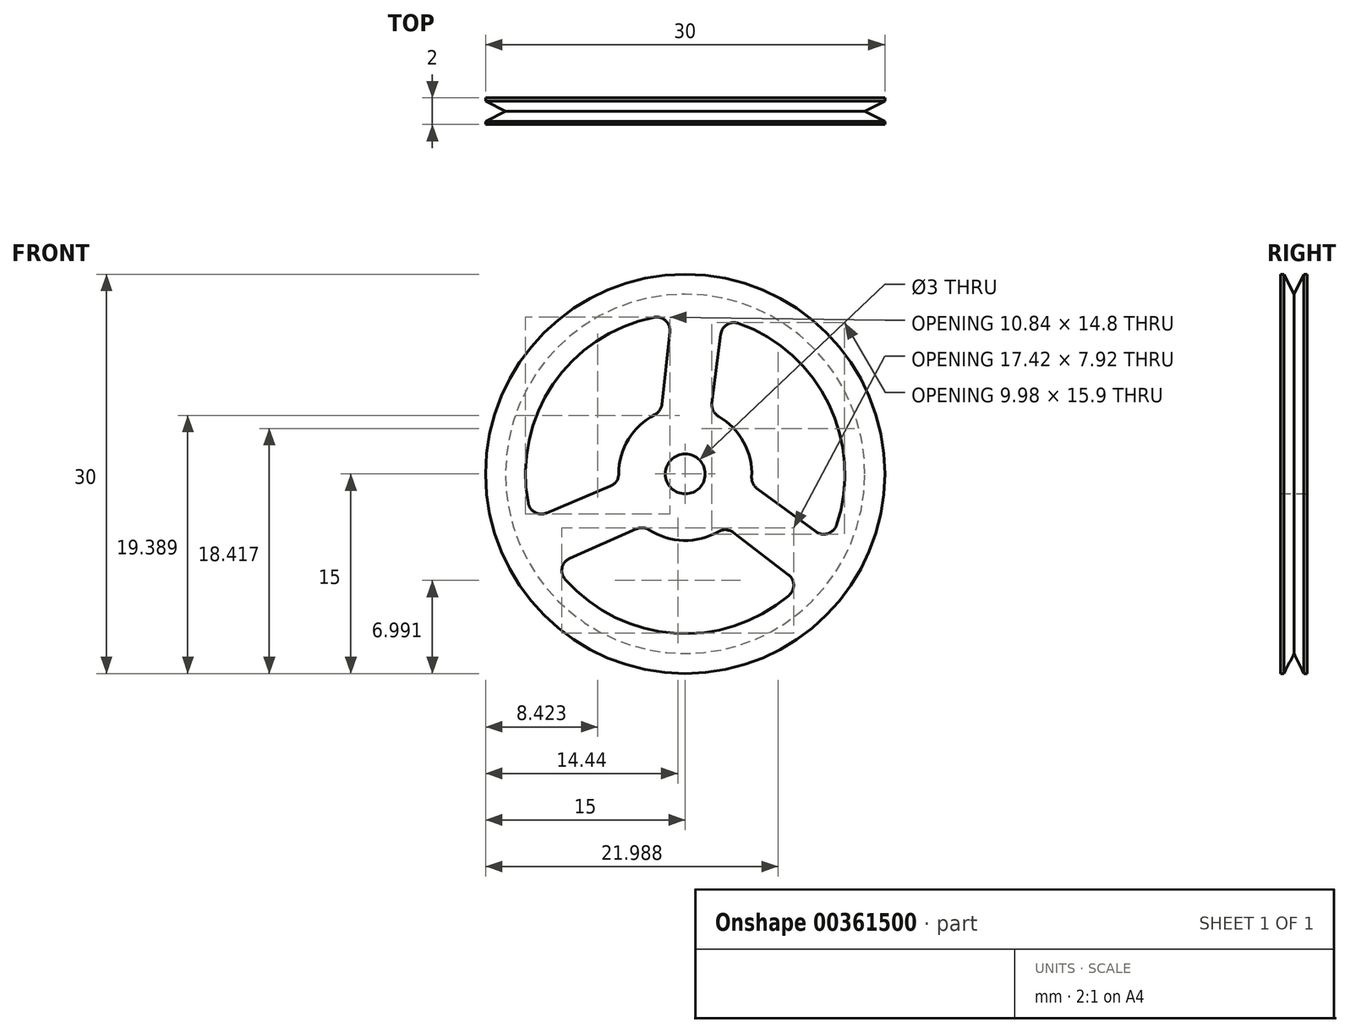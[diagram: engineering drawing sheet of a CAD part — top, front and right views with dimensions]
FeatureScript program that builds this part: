
annotation { "Feature Type Name" : "Feature", "Feature Type Description" : "" }
export const myFeature = defineFeature(function(context is Context, id is Id, definition is map)
    precondition{}
    {
        {
            var Q0;
            Q0=qCreatedBy(makeId("Front.planeOp"),FACE);
            var sketch = newSketch(context, id + "F0", { "sketchPlane" : qUnion([Q0])});
            skCircle(sketch, "E0", {"center": v(0, 0) * mm, "radius": 15 * mm});
            skArc(sketch, "E1.0", {"start": v(-2.34, 11.77) * mm, "mid": v(-9.94, 6.73) * mm, "end": v(-11.8, -2.2) * mm});
            skArc(sketch, "E2", {"start": v(-2.3, 4.44) * mm, "mid": v(-4.27, 2.6) * mm, "end": v(-5, 0) * mm});
            skCircle(sketch, "E3", {"center": v(0, 0) * mm, "radius": 1.5 * mm});
            skLineSegment(sketch, "E4.trimOffspring", {"start": v(-1.16, 10.68) * mm, "end": v(-1.76, 5.22) * mm});
            skLineSegment(sketch, "E5.trimOffspring", {"start": v(2.67, 10.5) * mm, "end": v(2, 5.32) * mm});
            skLineSegment(sketch, "E6.1.0", {"start": v(-10.43, -2.93) * mm, "end": v(-5.61, -0.92) * mm});
            skLineSegment(sketch, "E6.1.1", {"start": v(-8.67, -6.34) * mm, "end": v(-3.65, -4.13) * mm});
            skLineSegment(sketch, "E6.2.0", {"start": v(7.75, -7.57) * mm, "end": v(3.6, -4.4) * mm});
            skLineSegment(sketch, "E6.2.1", {"start": v(9.83, -4.34) * mm, "end": v(5.4, -1.1) * mm});
            skArc(sketch, "E7.trimOffspring", {"start": v(-2.7, -4.2) * mm, "mid": v(-0.12, -5) * mm, "end": v(2.5, -4.33) * mm});
            skArc(sketch, "E8.trimOffspring", {"start": v(-9.02, -7.91) * mm, "mid": v(-0.86, -11.97) * mm, "end": v(7.8, -9.12) * mm});
            skArc(sketch, "E9.trimOffspring", {"start": v(5, -0.24) * mm, "mid": v(4.39, 2.4) * mm, "end": v(2.5, 4.33) * mm});
            skArc(sketch, "E10.trimOffspring", {"start": v(11.36, -3.85) * mm, "mid": v(10.8, 5.24) * mm, "end": v(4, 11.31) * mm});
            skArc(sketch, "E11.filletArc", {"start": v(-1.16, 10.68) * mm, "mid": v(-1.47, 11.53) * mm, "end": v(-2.34, 11.77) * mm});
            skArc(sketch, "E12.filletArc", {"start": v(-2.3, 4.44) * mm, "mid": v(-1.93, 4.77) * mm, "end": v(-1.76, 5.22) * mm});
            skArc(sketch, "E13.filletArc", {"start": v(-5.61, -0.92) * mm, "mid": v(-5.17, -0.55) * mm, "end": v(-5, 0) * mm});
            skArc(sketch, "E14.filletArc", {"start": v(-11.8, -2.2) * mm, "mid": v(-11.3, -2.89) * mm, "end": v(-10.43, -2.93) * mm});
            skArc(sketch, "E15.filletArc", {"start": v(-8.67, -6.34) * mm, "mid": v(-9.24, -7.04) * mm, "end": v(-9.02, -7.91) * mm});
            skArc(sketch, "E16.filletArc", {"start": v(-2.7, -4.2) * mm, "mid": v(-3.16, -4.05) * mm, "end": v(-3.65, -4.13) * mm});
            skArc(sketch, "E17.filletArc", {"start": v(3.6, -4.4) * mm, "mid": v(3.06, -4.2) * mm, "end": v(2.5, -4.33) * mm});
            skArc(sketch, "E18.filletArc", {"start": v(7.8, -9.12) * mm, "mid": v(8.15, -8.33) * mm, "end": v(7.75, -7.57) * mm});
            skArc(sketch, "E19.filletArc", {"start": v(9.83, -4.34) * mm, "mid": v(10.72, -4.49) * mm, "end": v(11.36, -3.85) * mm});
            skArc(sketch, "E20.filletArc", {"start": v(5, -0.24) * mm, "mid": v(5.1, -0.72) * mm, "end": v(5.4, -1.1) * mm});
            skArc(sketch, "E21.filletArc", {"start": v(2, 5.32) * mm, "mid": v(2.1, 4.75) * mm, "end": v(2.5, 4.33) * mm});
            skArc(sketch, "E22.filletArc", {"start": v(4, 11.31) * mm, "mid": v(3.14, 11.22) * mm, "end": v(2.67, 10.5) * mm});
            skSolve(sketch);
        }
        {
            var Q0;
            Q0=makeQuery(id+"F0.imprint","IMPRINT",FACE,{"disambiguationData":[TD([[makeQuery(id+"F0.imprint","IMPRINT",EDGE,{"derivedFrom":sQuery(id+"F0.wireOp",EDGE,"E0")}),1.0]])]});
            extrude(context, id + "F1", {"entities" : qUnion([Q0]), "endBound" : BoundingType.SYMMETRIC, "depth" : 2 * mm});
        }
        {
            var Q0;
            Q0=qCreatedBy(makeId("Right.planeOp"),FACE);
            var sketch = newSketch(context, id + "F2", { "sketchPlane" : qUnion([Q0])});
            skLineSegment(sketch, "E23", {"start": v(0, 13.5) * mm, "end": v(0, 15) * mm});
            skLineSegment(sketch, "E24", {"start": v(0, 15) * mm, "end": v(0.75, 15) * mm});
            skLineSegment(sketch, "E25", {"start": v(0.75, 15) * mm, "end": v(0, 13.5) * mm});
            skLineSegment(sketch, "E26.MirrorCS", {"start": v(-0.75, 15) * mm, "end": v(0, 13.5) * mm});
            skLineSegment(sketch, "E27.MirrorCS", {"start": v(0, 15) * mm, "end": v(-0.75, 15) * mm});
            skLineSegment(sketch, "E28", {"start": v(12.17, 0) * mm, "end": v(-12.06, 0) * mm, "construction": true});
            skSolve(sketch);
        }
        {
            var Q0;
            Q0 = qSketchRegion(id + "F2", true);
            var Q1;
            Q1=sQuery(id+"F2.wireOp",EDGE,"E28");
            revolve(context, id + "F3", {"operationType" : NewBodyOperationType.REMOVE, "entities" : qUnion([Q0]), "axis" : qUnion([Q1]), "revolveType" : RevolveType.FULL, "oppositeDirection" : true});
        }
    });
